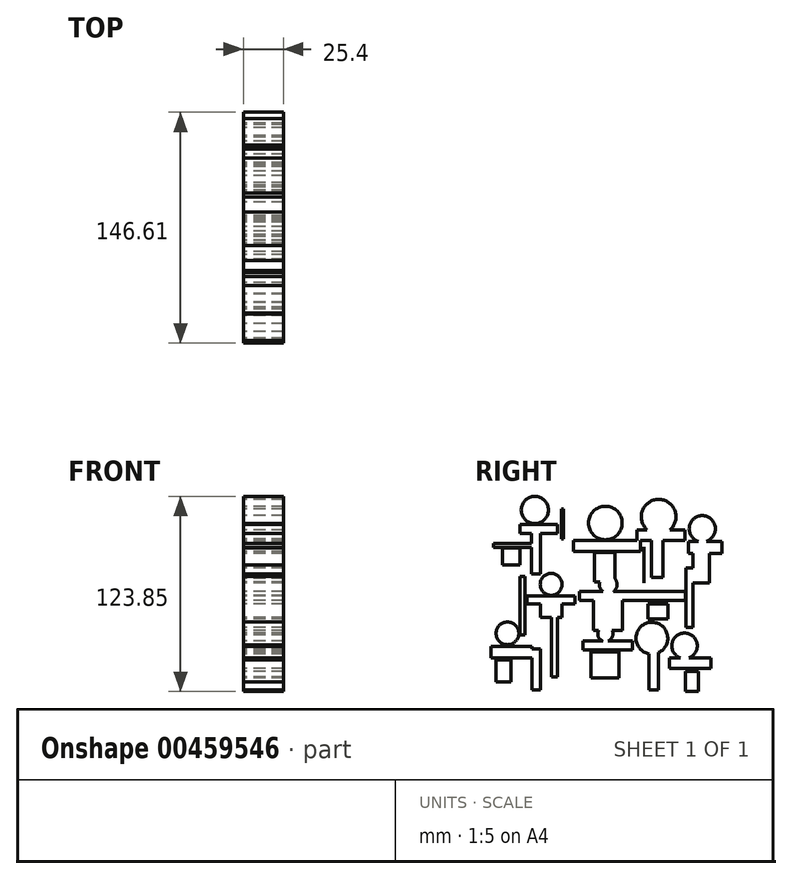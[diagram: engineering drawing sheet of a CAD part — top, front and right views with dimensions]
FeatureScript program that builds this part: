
annotation { "Feature Type Name" : "Feature", "Feature Type Description" : "" }
export const myFeature = defineFeature(function(context is Context, id is Id, definition is map)
    precondition{}
    {
        {
            var Q0;
            Q0=qCreatedBy(makeId("Right.planeOp"),FACE);
            var sketch = newSketch(context, id + "F0", { "sketchPlane" : qUnion([Q0])});
            skLineSegment(sketch, "E0.bottom", {"start": v(-46.63, -50.44) * mm, "end": v(-41.15, -50.44) * mm});
            skLineSegment(sketch, "E0.top", {"start": v(-46.63, -24.23) * mm, "end": v(-41.15, -24.23) * mm});
            skLineSegment(sketch, "E0.left", {"start": v(-46.63, -50.44) * mm, "end": v(-46.63, -24.23) * mm});
            skLineSegment(sketch, "E0.right", {"start": v(-41.15, -50.44) * mm, "end": v(-41.15, -24.23) * mm});
            skLineSegment(sketch, "E1.bottom", {"start": v(-46.94, 49.23) * mm, "end": v(-41.15, 49.23) * mm});
            skLineSegment(sketch, "E1.top", {"start": v(-46.94, 23.32) * mm, "end": v(-41.15, 23.32) * mm});
            skLineSegment(sketch, "E1.left", {"start": v(-46.94, 49.23) * mm, "end": v(-46.94, 23.32) * mm});
            skLineSegment(sketch, "E1.right", {"start": v(-41.15, 49.23) * mm, "end": v(-41.15, 23.32) * mm});
            skLineSegment(sketch, "E2.bottom", {"start": v(29.26, 44.96) * mm, "end": v(36.58, 44.96) * mm});
            skLineSegment(sketch, "E2.top", {"start": v(29.26, 21.18) * mm, "end": v(36.58, 21.18) * mm});
            skLineSegment(sketch, "E2.left", {"start": v(29.26, 44.96) * mm, "end": v(29.26, 21.18) * mm});
            skLineSegment(sketch, "E2.right", {"start": v(36.58, 44.96) * mm, "end": v(36.58, 21.18) * mm});
            skLineSegment(sketch, "E3.bottom", {"start": v(27.74, -26.67) * mm, "end": v(33.83, -26.67) * mm});
            skLineSegment(sketch, "E3.top", {"start": v(27.74, -50.44) * mm, "end": v(33.83, -50.44) * mm});
            skLineSegment(sketch, "E3.left", {"start": v(27.74, -26.67) * mm, "end": v(27.74, -50.44) * mm});
            skLineSegment(sketch, "E3.right", {"start": v(33.83, -26.67) * mm, "end": v(33.83, -50.44) * mm});
            skLineSegment(sketch, "E4.bottom", {"start": v(-7.62, 6.55) * mm, "end": v(10.97, 6.55) * mm});
            skLineSegment(sketch, "E4.top", {"start": v(-7.62, -12.65) * mm, "end": v(10.97, -12.65) * mm});
            skLineSegment(sketch, "E4.left", {"start": v(-7.62, 6.55) * mm, "end": v(-7.62, -12.65) * mm});
            skLineSegment(sketch, "E4.right", {"start": v(10.97, 6.55) * mm, "end": v(10.97, -12.65) * mm});
            skLineSegment(sketch, "E5.bottom", {"start": v(-60.05, -31.24) * mm, "end": v(-69.5, -31.24) * mm});
            skLineSegment(sketch, "E5.top", {"start": v(-60.05, -45.26) * mm, "end": v(-69.5, -45.26) * mm});
            skLineSegment(sketch, "E5.left", {"start": v(-60.05, -31.24) * mm, "end": v(-60.05, -45.26) * mm});
            skLineSegment(sketch, "E5.right", {"start": v(-69.5, -31.24) * mm, "end": v(-69.5, -45.26) * mm});
            skPoint(sketch, "E6.firstSnap0", {"position": v(27.74, -38.56) * mm});
            skLineSegment(sketch, "E6.bottom", {"start": v(50.9, -38.56) * mm, "end": v(59.13, -38.56) * mm});
            skLineSegment(sketch, "E6.top", {"start": v(50.9, -51.36) * mm, "end": v(59.13, -51.36) * mm});
            skLineSegment(sketch, "E6.left", {"start": v(50.9, -38.56) * mm, "end": v(50.9, -51.36) * mm});
            skLineSegment(sketch, "E6.right", {"start": v(59.13, -38.56) * mm, "end": v(59.13, -51.36) * mm});
            skLineSegment(sketch, "E7.bottom", {"start": v(55.78, 36.42) * mm, "end": v(66.14, 36.42) * mm});
            skLineSegment(sketch, "E7.top", {"start": v(55.78, 17.53) * mm, "end": v(66.14, 17.53) * mm});
            skLineSegment(sketch, "E7.left", {"start": v(55.78, 36.42) * mm, "end": v(55.78, 17.53) * mm});
            skLineSegment(sketch, "E7.right", {"start": v(66.14, 36.42) * mm, "end": v(66.14, 17.53) * mm});
            skLineSegment(sketch, "E8.bottom", {"start": v(-54.25, 39.78) * mm, "end": v(-65.23, 39.78) * mm});
            skLineSegment(sketch, "E8.top", {"start": v(-54.25, 29.1) * mm, "end": v(-65.23, 29.1) * mm});
            skLineSegment(sketch, "E8.left", {"start": v(-54.25, 39.78) * mm, "end": v(-54.25, 29.1) * mm});
            skLineSegment(sketch, "E8.right", {"start": v(-65.23, 39.78) * mm, "end": v(-65.23, 29.1) * mm});
            skLineSegment(sketch, "E9.bottom", {"start": v(-41.15, 4.11) * mm, "end": v(-27.43, 4.11) * mm});
            skLineSegment(sketch, "E9.top", {"start": v(-41.15, -4.42) * mm, "end": v(-27.43, -4.42) * mm});
            skLineSegment(sketch, "E9.left", {"start": v(-41.15, 4.11) * mm, "end": v(-41.15, -4.42) * mm});
            skLineSegment(sketch, "E9.right", {"start": v(-27.43, 4.11) * mm, "end": v(-27.43, -4.42) * mm});
            skLineSegment(sketch, "E10.bottom", {"start": v(-7.01, 37.03) * mm, "end": v(6.1, 37.03) * mm});
            skLineSegment(sketch, "E10.top", {"start": v(-7.01, 18.14) * mm, "end": v(6.1, 18.14) * mm});
            skLineSegment(sketch, "E10.left", {"start": v(-7.01, 37.03) * mm, "end": v(-7.01, 18.14) * mm});
            skLineSegment(sketch, "E10.right", {"start": v(6.1, 37.03) * mm, "end": v(6.1, 18.14) * mm});
            skLineSegment(sketch, "E11.bottom", {"start": v(0, -25.15) * mm, "end": v(0, -25.15) * mm});
            skLineSegment(sketch, "E11.top", {"start": v(0, -42.82) * mm, "end": v(0, -42.82) * mm});
            skLineSegment(sketch, "E11.left", {"start": v(0, -25.15) * mm, "end": v(0, -42.82) * mm});
            skLineSegment(sketch, "E11.right", {"start": v(0, -25.15) * mm, "end": v(0, -42.82) * mm});
            skLineSegment(sketch, "E12.bottom", {"start": v(-9.14, -26.37) * mm, "end": v(8.53, -26.37) * mm});
            skLineSegment(sketch, "E12.top", {"start": v(-9.14, -42.82) * mm, "end": v(8.53, -42.82) * mm});
            skLineSegment(sketch, "E12.left", {"start": v(-9.14, -26.37) * mm, "end": v(-9.14, -42.82) * mm});
            skLineSegment(sketch, "E12.right", {"start": v(8.53, -26.37) * mm, "end": v(8.53, -42.82) * mm});
            skLineSegment(sketch, "E13.bottom", {"start": v(27.13, 4.11) * mm, "end": v(39.62, 4.11) * mm});
            skLineSegment(sketch, "E13.top", {"start": v(27.13, -5.33) * mm, "end": v(39.62, -5.33) * mm});
            skLineSegment(sketch, "E13.left", {"start": v(27.13, 4.11) * mm, "end": v(27.13, -5.33) * mm});
            skLineSegment(sketch, "E13.right", {"start": v(39.62, 4.11) * mm, "end": v(39.62, -5.33) * mm});
            skLineSegment(sketch, "E14.bottom", {"start": v(-20.12, 44.65) * mm, "end": v(22.25, 44.65) * mm});
            skLineSegment(sketch, "E14.top", {"start": v(-20.12, 37.64) * mm, "end": v(22.25, 37.64) * mm});
            skLineSegment(sketch, "E14.left", {"start": v(-20.12, 44.65) * mm, "end": v(-20.12, 37.64) * mm});
            skLineSegment(sketch, "E14.right", {"start": v(22.25, 44.65) * mm, "end": v(22.25, 37.64) * mm});
            skLineSegment(sketch, "E15.bottom", {"start": v(-14.33, -19.35) * mm, "end": v(17.07, -19.35) * mm});
            skLineSegment(sketch, "E15.top", {"start": v(-14.33, -25.15) * mm, "end": v(17.07, -25.15) * mm});
            skLineSegment(sketch, "E15.left", {"start": v(-14.33, -19.35) * mm, "end": v(-14.33, -25.15) * mm});
            skLineSegment(sketch, "E15.right", {"start": v(17.07, -19.35) * mm, "end": v(17.07, -25.15) * mm});
            skLineSegment(sketch, "E16.bottom", {"start": v(-16.46, 12.04) * mm, "end": v(50.9, 12.04) * mm});
            skLineSegment(sketch, "E16.top", {"start": v(-16.46, 6.55) * mm, "end": v(50.9, 6.55) * mm});
            skLineSegment(sketch, "E16.left", {"start": v(-16.46, 12.04) * mm, "end": v(-16.46, 6.55) * mm});
            skLineSegment(sketch, "E16.right", {"start": v(50.9, 12.04) * mm, "end": v(50.9, 6.55) * mm});
            skLineSegment(sketch, "E17.bottom", {"start": v(40.84, -30.02) * mm, "end": v(67.06, -30.02) * mm});
            skLineSegment(sketch, "E17.top", {"start": v(40.84, -36.73) * mm, "end": v(67.06, -36.73) * mm});
            skLineSegment(sketch, "E17.left", {"start": v(40.84, -30.02) * mm, "end": v(40.84, -36.73) * mm});
            skLineSegment(sketch, "E17.right", {"start": v(67.06, -30.02) * mm, "end": v(67.06, -36.73) * mm});
            skLineSegment(sketch, "E18.bottom", {"start": v(-72.54, -22.7) * mm, "end": v(-46.63, -22.7) * mm});
            skLineSegment(sketch, "E18.top", {"start": v(-72.54, -30.02) * mm, "end": v(-46.63, -30.02) * mm});
            skLineSegment(sketch, "E18.left", {"start": v(-72.54, -22.7) * mm, "end": v(-72.54, -30.02) * mm});
            skLineSegment(sketch, "E18.right", {"start": v(-46.63, -22.7) * mm, "end": v(-46.63, -30.02) * mm});
            skLineSegment(sketch, "E19.bottom", {"start": v(-49.68, 9.3) * mm, "end": v(-19.2, 9.3) * mm});
            skLineSegment(sketch, "E19.top", {"start": v(-49.68, 4.11) * mm, "end": v(-19.2, 4.11) * mm});
            skLineSegment(sketch, "E19.left", {"start": v(-49.68, 9.3) * mm, "end": v(-49.68, 4.11) * mm});
            skLineSegment(sketch, "E19.right", {"start": v(-19.2, 9.3) * mm, "end": v(-19.2, 4.11) * mm});
            skLineSegment(sketch, "E20.bottom", {"start": v(52.73, 44.04) * mm, "end": v(74.07, 44.04) * mm});
            skLineSegment(sketch, "E20.top", {"start": v(52.73, 36.42) * mm, "end": v(74.07, 36.42) * mm});
            skLineSegment(sketch, "E20.left", {"start": v(52.73, 44.04) * mm, "end": v(52.73, 36.42) * mm});
            skLineSegment(sketch, "E20.right", {"start": v(74.07, 44.04) * mm, "end": v(74.07, 36.42) * mm});
            skLineSegment(sketch, "E21.bottom", {"start": v(20.12, 51.36) * mm, "end": v(50.6, 51.36) * mm});
            skLineSegment(sketch, "E21.top", {"start": v(20.12, 44.65) * mm, "end": v(50.6, 44.65) * mm});
            skLineSegment(sketch, "E21.left", {"start": v(20.12, 51.36) * mm, "end": v(20.12, 44.65) * mm});
            skLineSegment(sketch, "E21.right", {"start": v(50.6, 51.36) * mm, "end": v(50.6, 44.65) * mm});
            skLineSegment(sketch, "E22.bottom", {"start": v(-54.25, 54.71) * mm, "end": v(-30.48, 54.71) * mm});
            skLineSegment(sketch, "E22.top", {"start": v(-54.25, 48.92) * mm, "end": v(-30.48, 48.92) * mm});
            skLineSegment(sketch, "E22.left", {"start": v(-54.25, 54.71) * mm, "end": v(-54.25, 48.92) * mm});
            skLineSegment(sketch, "E22.right", {"start": v(-30.48, 54.71) * mm, "end": v(-30.48, 48.92) * mm});
            skLineSegment(sketch, "E23.bottom", {"start": v(-71.02, 42.52) * mm, "end": v(-46.94, 42.52) * mm});
            skLineSegment(sketch, "E23.top", {"start": v(-71.02, 40.08) * mm, "end": v(-46.94, 40.08) * mm});
            skLineSegment(sketch, "E23.left", {"start": v(-71.02, 42.52) * mm, "end": v(-71.02, 40.08) * mm});
            skLineSegment(sketch, "E23.right", {"start": v(-46.94, 42.52) * mm, "end": v(-46.94, 40.08) * mm});
            skCircle(sketch, "E24", {"center": v(0, 55.63) * mm, "radius": 10.66 * mm});
            skCircle(sketch, "E25", {"center": v(33.83, 59.59) * mm, "radius": 11.01 * mm});
            skCircle(sketch, "E26", {"center": v(61.57, 51.97) * mm, "radius": 8.33 * mm});
            skCircle(sketch, "E27", {"center": v(-44.8, 63.86) * mm, "radius": 8.63 * mm});
            skCircle(sketch, "E28", {"center": v(-34.44, 16.61) * mm, "radius": 6.96 * mm});
            skCircle(sketch, "E29", {"center": v(1.83, 16.61) * mm, "radius": 5.62 * mm});
            skCircle(sketch, "E30", {"center": v(0, -14.78) * mm, "radius": 4.82 * mm});
            skCircle(sketch, "E31", {"center": v(-62.18, -14.48) * mm, "radius": 7.23 * mm});
            skCircle(sketch, "E32", {"center": v(50.3, -22.4) * mm, "radius": 8.1 * mm});
            skCircle(sketch, "E33", {"center": v(29.57, -17.53) * mm, "radius": 10.1 * mm});
            skLineSegment(sketch, "E34.bottom", {"start": v(-27.74, 64.47) * mm, "end": v(-26.52, 64.47) * mm});
            skLineSegment(sketch, "E34.top", {"start": v(-27.74, 45.57) * mm, "end": v(-26.52, 45.57) * mm});
            skLineSegment(sketch, "E34.left", {"start": v(-27.74, 64.47) * mm, "end": v(-27.74, 45.57) * mm});
            skLineSegment(sketch, "E34.right", {"start": v(-26.52, 64.47) * mm, "end": v(-26.52, 45.57) * mm});
            skLineSegment(sketch, "E35.bottom", {"start": v(-54.25, 21.8) * mm, "end": v(-50.9, 21.8) * mm});
            skLineSegment(sketch, "E35.top", {"start": v(-54.25, -15.4) * mm, "end": v(-50.9, -15.4) * mm});
            skLineSegment(sketch, "E35.left", {"start": v(-54.25, 21.8) * mm, "end": v(-54.25, -15.4) * mm});
            skLineSegment(sketch, "E35.right", {"start": v(-50.9, 21.8) * mm, "end": v(-50.9, -15.4) * mm});
            skPoint(sketch, "E36.firstSnap0", {"position": v(55.78, 26.97) * mm});
            skLineSegment(sketch, "E36.bottom", {"start": v(51.2, 26.97) * mm, "end": v(55.78, 26.97) * mm});
            skLineSegment(sketch, "E36.top", {"start": v(51.2, -10.82) * mm, "end": v(55.78, -10.82) * mm});
            skLineSegment(sketch, "E36.left", {"start": v(51.2, 26.97) * mm, "end": v(51.2, -10.82) * mm});
            skLineSegment(sketch, "E36.right", {"start": v(55.78, 26.97) * mm, "end": v(55.78, -10.82) * mm});
            skLineSegment(sketch, "E37.bottom", {"start": v(24.38, 40.39) * mm, "end": v(24.69, 40.39) * mm});
            skLineSegment(sketch, "E37.top", {"start": v(24.38, 17.53) * mm, "end": v(24.69, 17.53) * mm});
            skLineSegment(sketch, "E37.left", {"start": v(24.38, 40.39) * mm, "end": v(24.38, 17.53) * mm});
            skLineSegment(sketch, "E37.right", {"start": v(24.69, 40.39) * mm, "end": v(24.69, 17.53) * mm});
            skLineSegment(sketch, "E38.bottom", {"start": v(-34.29, -4.42) * mm, "end": v(-30.48, -4.42) * mm});
            skLineSegment(sketch, "E38.top", {"start": v(-34.29, -42.21) * mm, "end": v(-30.48, -42.21) * mm});
            skLineSegment(sketch, "E38.left", {"start": v(-34.29, -4.42) * mm, "end": v(-34.29, -42.21) * mm});
            skLineSegment(sketch, "E38.right", {"start": v(-30.48, -4.42) * mm, "end": v(-30.48, -42.21) * mm});
            skSolve(sketch);
        }
        {
            var Q0;
            Q0 = qSketchRegion(id + "F0", true);
            extrude(context, id + "F1", {"entities" : qUnion([Q0]), "depth" : 25.4 * mm});
        }
        {
            var Q0;
            Q0 = qSketchRegion(id + "F0", true);
            extrude(context, id + "F2", {"entities" : qUnion([Q0]), "depth" : 25.4 * mm});
        }
        {
            var Q0;
            Q0 = qSketchRegion(id + "F0", true);
            extrude(context, id + "F3", {"entities" : qUnion([Q0]), "depth" : 25.4 * mm});
        }
        {
            var Q0;
            Q0 = qSketchRegion(id + "F0", true);
            extrude(context, id + "F4", {"entities" : qUnion([Q0]), "depth" : 25.4 * mm});
        }
    });
